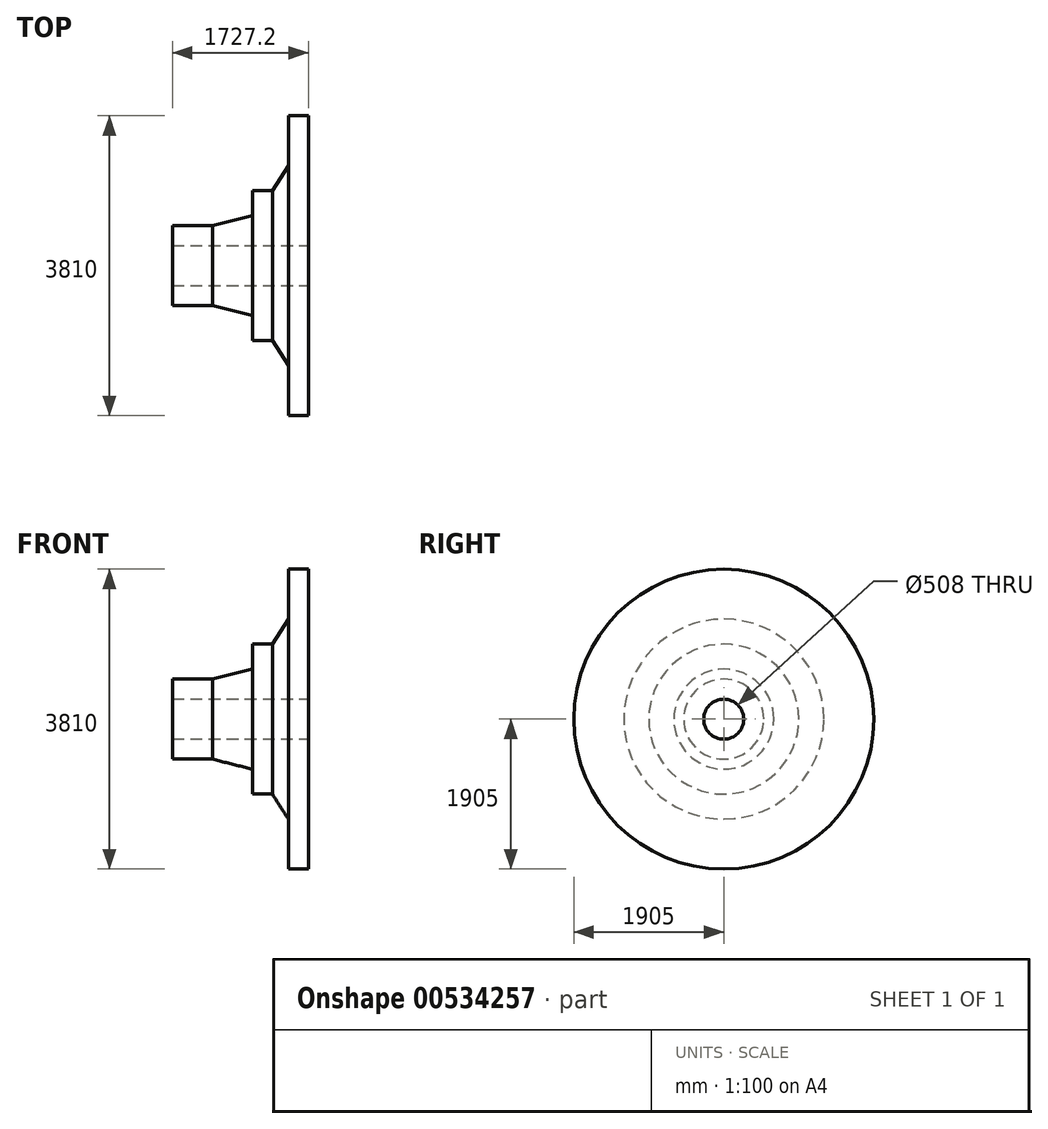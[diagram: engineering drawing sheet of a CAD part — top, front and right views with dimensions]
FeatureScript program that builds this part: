
annotation { "Feature Type Name" : "Feature", "Feature Type Description" : "" }
export const myFeature = defineFeature(function(context is Context, id is Id, definition is map)
    precondition{}
    {
        {
            var Q0;
            Q0=qCreatedBy(makeId("Front.planeOp"),FACE);
            var sketch = newSketch(context, id + "F0", { "sketchPlane" : qUnion([Q0])});
            skLineSegment(sketch, "E0", {"start": v(1844.87, 0) * mm, "end": v(-1873.25, 0) * mm});
            skLineSegment(sketch, "E1", {"start": v(1771.18, 254) * mm, "end": v(43.98, 254) * mm});
            skLineSegment(sketch, "E2", {"start": v(1771.18, 254) * mm, "end": v(1771.18, 1905) * mm});
            skLineSegment(sketch, "E3", {"start": v(1771.18, 1905) * mm, "end": v(1517.18, 1905) * mm});
            skLineSegment(sketch, "E4", {"start": v(1517.18, 1905) * mm, "end": v(1517.18, 1270) * mm});
            skLineSegment(sketch, "E5", {"start": v(1517.18, 1270) * mm, "end": v(1313.98, 952.5) * mm});
            skLineSegment(sketch, "E6", {"start": v(1313.98, 952.5) * mm, "end": v(1059.98, 952.5) * mm});
            skLineSegment(sketch, "E7", {"start": v(1059.98, 952.5) * mm, "end": v(1059.98, 635) * mm});
            skLineSegment(sketch, "E8", {"start": v(1059.98, 635) * mm, "end": v(551.98, 508) * mm});
            skLineSegment(sketch, "E9", {"start": v(551.98, 508) * mm, "end": v(43.98, 508) * mm});
            skLineSegment(sketch, "E10", {"start": v(43.98, 508) * mm, "end": v(43.98, 254) * mm});
            skSolve(sketch);
        }
        {
            var Q0;
            Q0 = qSketchRegion(id + "F0", true);
            var Q1;
            Q1=sQuery(id+"F0.wireOp",EDGE,"E0");
            revolve(context, id + "F1", {"entities" : qUnion([Q0]), "axis" : qUnion([Q1]), "revolveType" : RevolveType.FULL});
        }
    });
